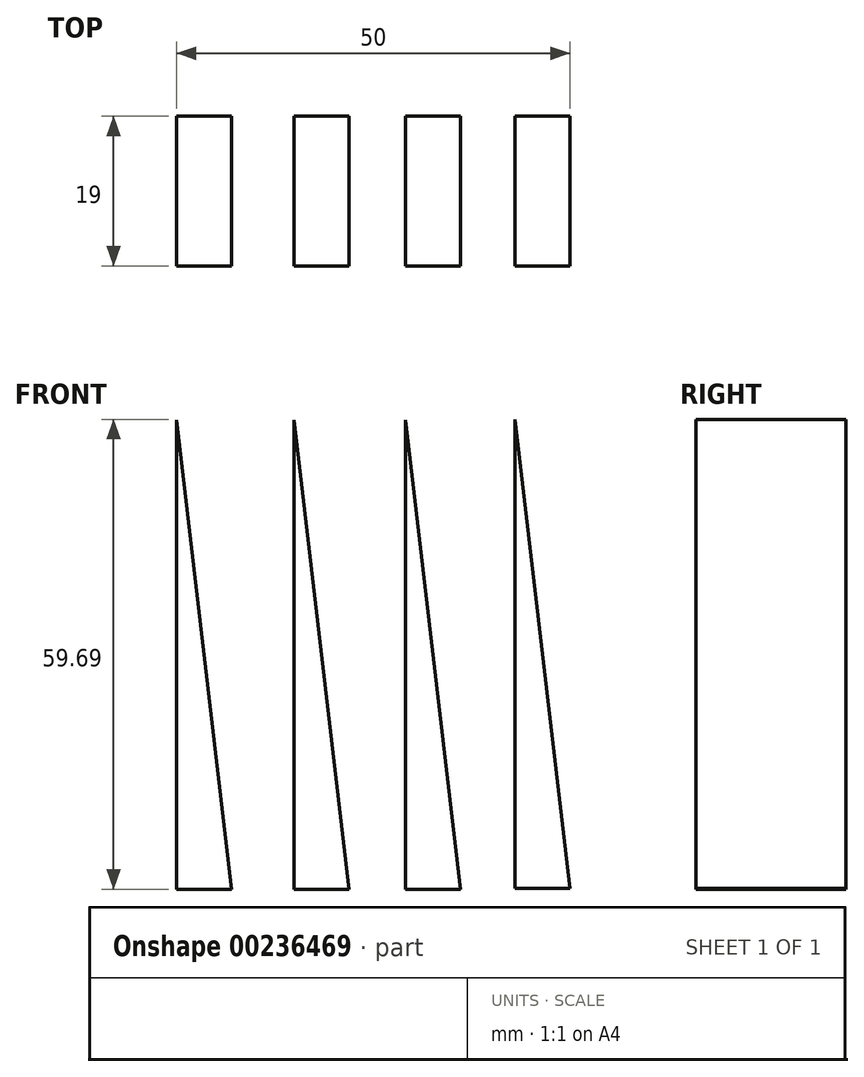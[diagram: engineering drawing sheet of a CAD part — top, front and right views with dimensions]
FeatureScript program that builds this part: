
annotation { "Feature Type Name" : "Feature", "Feature Type Description" : "" }
export const myFeature = defineFeature(function(context is Context, id is Id, definition is map)
    precondition{}
    {
        {
            var Q0;
            Q0=qCreatedBy(makeId("Front.planeOp"),FACE);
            var sketch = newSketch(context, id + "F0", { "sketchPlane" : qUnion([Q0])});
            skLineSegment(sketch, "E0", {"start": v(0, 0) * mm, "end": v(7, 0) * mm});
            skLineSegment(sketch, "E1", {"start": v(7, 0) * mm, "end": v(0, 59.6) * mm});
            skLineSegment(sketch, "E2", {"start": v(0, 59.6) * mm, "end": v(0, 0) * mm});
            skSolve(sketch);
        }
        {
            var Q0;
            Q0=makeQuery(id+"F0.imprint","IMPRINT",FACE,{"disambiguationData":[TD([[makeQuery(id+"F0.imprint","IMPRINT",EDGE,{"derivedFrom":sQuery(id+"F0.wireOp",EDGE,"E0")}),1.0]])]});
            extrude(context, id + "F1", {"entities" : qUnion([Q0]), "depth" : 19 * mm, "offsetDistance" : 25 * mm});
        }
        {
            var Q0;
            Q0=makeQuery(id+"F1.opExtrude","SWEPT_BODY",BODY,{"disambiguationData":[OSD([sQuery(id+"F0.wireOp",EDGE,"E0"),sQuery(id+"F0.wireOp",EDGE,"E1"),sQuery(id+"F0.wireOp",EDGE,"E2")])]});
            transform(context, id + "F2", {"entities" : qUnion([Q0]), "transformType" : TransformType.TRANSLATION_3D, "dx" : 13.9 * mm, "dy" : 0 * mm, "dz" : 0.1 * mm, "makeCopy" : true});
        }
        {
            var Q0;
            Q0=makeQuery(id+"F1.opExtrude","SWEPT_BODY",BODY,{"disambiguationData":[OSD([sQuery(id+"F0.wireOp",EDGE,"E0"),sQuery(id+"F0.wireOp",EDGE,"E1"),sQuery(id+"F0.wireOp",EDGE,"E2")])]});
            transform(context, id + "F3", {"entities" : qUnion([Q0]), "transformType" : TransformType.TRANSLATION_3D, "dx" : -14.2 * mm, "dy" : 0 * mm, "dz" : 0 * mm, "makeCopy" : true});
        }
        {
            var Q0;
            Q0=makeQuery(id+"F1.opExtrude","SWEPT_BODY",BODY,{"disambiguationData":[OSD([sQuery(id+"F0.wireOp",EDGE,"E0"),sQuery(id+"F0.wireOp",EDGE,"E1"),sQuery(id+"F0.wireOp",EDGE,"E2")])]});
            transform(context, id + "F4", {"entities" : qUnion([Q0]), "transformType" : TransformType.TRANSLATION_3D, "dx" : -29.1 * mm, "dy" : 0 * mm, "dz" : 0 * mm, "makeCopy" : true});
        }
    });
